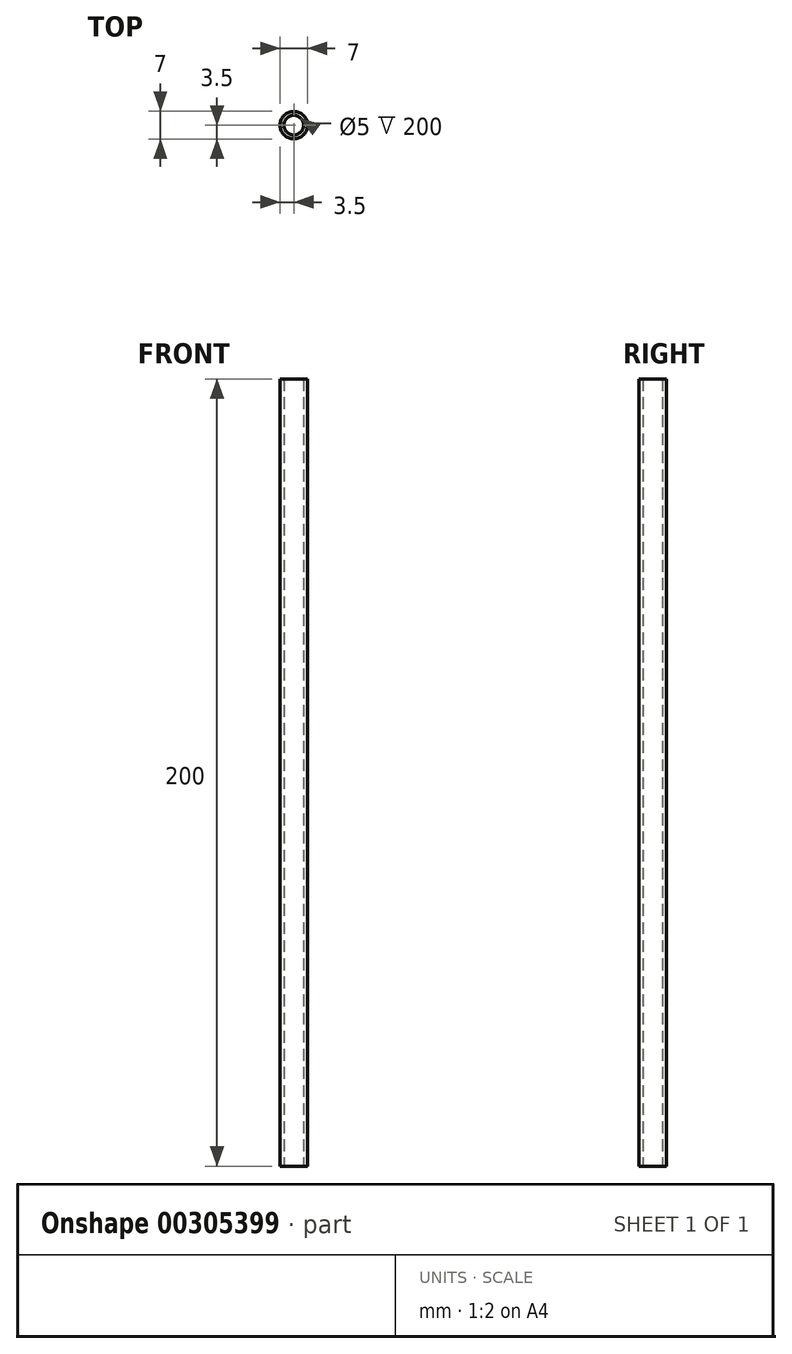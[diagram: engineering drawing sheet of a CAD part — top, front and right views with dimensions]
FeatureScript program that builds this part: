
annotation { "Feature Type Name" : "Feature", "Feature Type Description" : "" }
export const myFeature = defineFeature(function(context is Context, id is Id, definition is map)
    precondition{}
    {
        {
            var Q0;
            Q0=qCreatedBy(makeId("Front.planeOp"),FACE);
            var sketch = newSketch(context, id + "F0", { "sketchPlane" : qUnion([Q0])});
            skLineSegment(sketch, "E0", {"start": v(0, 0) * mm, "end": v(0, 200) * mm, "construction": true});
            skLineSegment(sketch, "E1.bottom", {"start": v(-3.5, 0) * mm, "end": v(-2.5, 0) * mm});
            skLineSegment(sketch, "E1.top", {"start": v(-3.5, 200) * mm, "end": v(-2.5, 200) * mm});
            skLineSegment(sketch, "E1.left", {"start": v(-3.5, 0) * mm, "end": v(-3.5, 200) * mm});
            skLineSegment(sketch, "E1.right", {"start": v(-2.5, 0) * mm, "end": v(-2.5, 200) * mm});
            skSolve(sketch);
        }
        {
            var Q0;
            Q0 = qSketchRegion(id + "F0", true);
            var Q1;
            Q1=sQuery(id+"F0.wireOp",EDGE,"E0");
            revolve(context, id + "F1", {"entities" : qUnion([Q0]), "axis" : qUnion([Q1]), "revolveType" : RevolveType.FULL});
        }
    });
